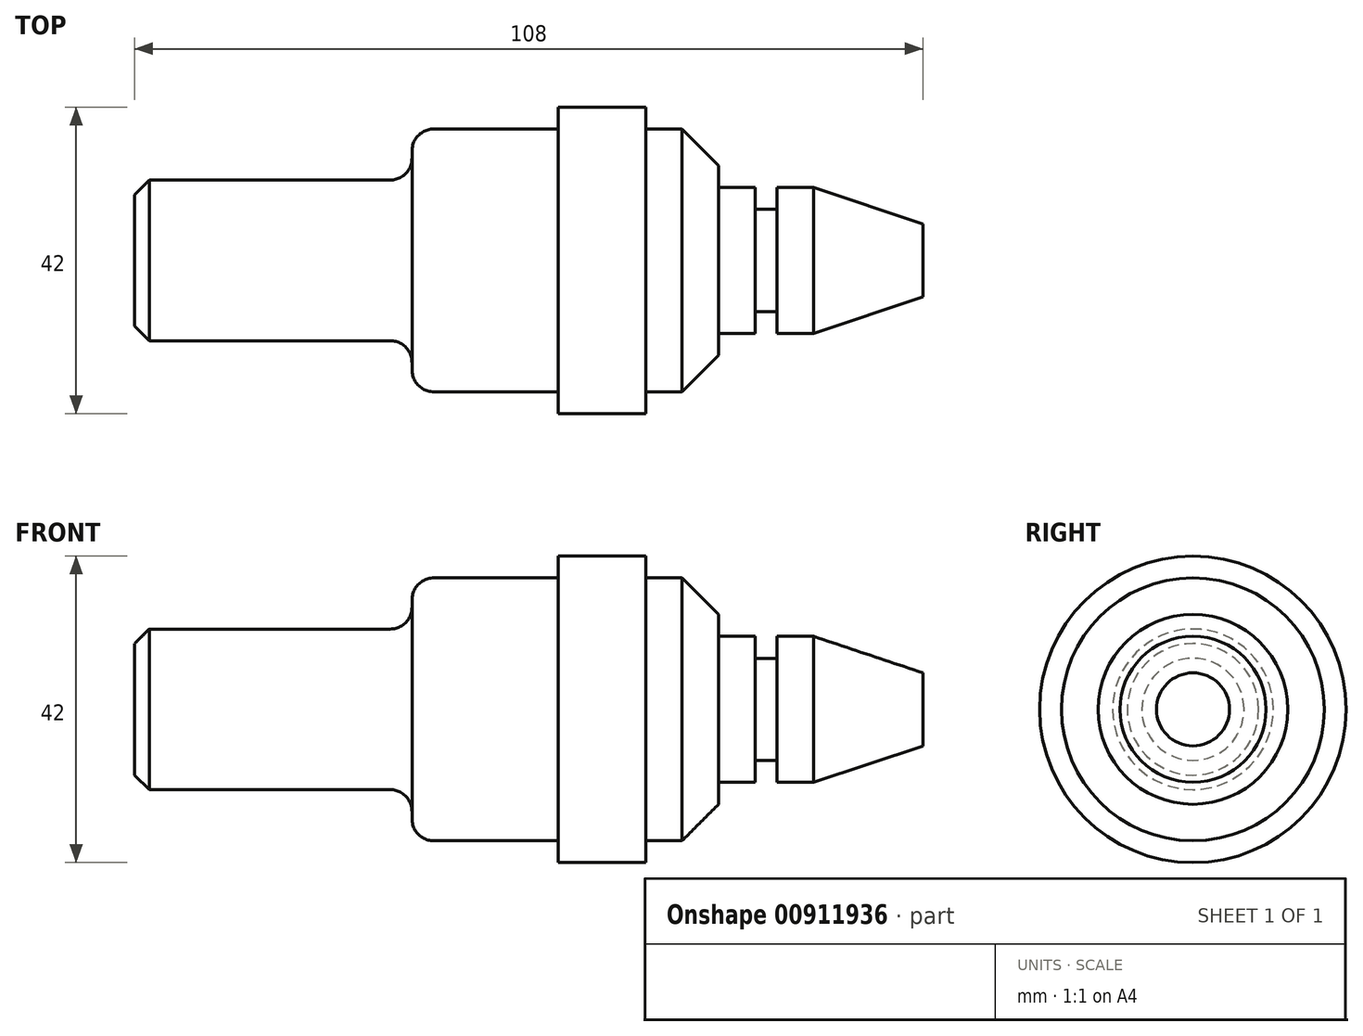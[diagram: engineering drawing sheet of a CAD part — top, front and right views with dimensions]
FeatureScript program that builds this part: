
annotation { "Feature Type Name" : "Feature", "Feature Type Description" : "" }
export const myFeature = defineFeature(function(context is Context, id is Id, definition is map)
    precondition{}
    {
        {
            var Q0;
            Q0=qCreatedBy(makeId("Top.planeOp"),FACE);
            var sketch = newSketch(context, id + "F0", { "sketchPlane" : qUnion([Q0])});
            skLineSegment(sketch, "E0", {"start": v(-211.25, 52.42) * mm, "end": v(-103.25, 52.42) * mm});
            skLineSegment(sketch, "E1", {"start": v(-211.25, 52.42) * mm, "end": v(-211.25, 41.42) * mm});
            skLineSegment(sketch, "E2", {"start": v(-211.25, 41.42) * mm, "end": v(-173.25, 41.42) * mm});
            skLineSegment(sketch, "E3", {"start": v(-173.25, 41.42) * mm, "end": v(-173.25, 34.42) * mm});
            skLineSegment(sketch, "E4", {"start": v(-173.25, 34.42) * mm, "end": v(-153.25, 34.42) * mm});
            skLineSegment(sketch, "E5", {"start": v(-153.25, 34.42) * mm, "end": v(-153.25, 31.42) * mm});
            skLineSegment(sketch, "E6", {"start": v(-153.25, 31.42) * mm, "end": v(-141.25, 31.42) * mm});
            skLineSegment(sketch, "E7", {"start": v(-141.25, 31.42) * mm, "end": v(-141.25, 34.42) * mm});
            skLineSegment(sketch, "E8", {"start": v(-141.25, 34.42) * mm, "end": v(-131.25, 34.42) * mm});
            skLineSegment(sketch, "E9", {"start": v(-131.25, 34.42) * mm, "end": v(-131.25, 42.42) * mm});
            skLineSegment(sketch, "E10", {"start": v(-131.25, 42.42) * mm, "end": v(-126.25, 42.42) * mm});
            skLineSegment(sketch, "E11", {"start": v(-126.25, 42.42) * mm, "end": v(-126.25, 45.42) * mm});
            skLineSegment(sketch, "E12", {"start": v(-126.25, 45.42) * mm, "end": v(-123.25, 45.42) * mm});
            skLineSegment(sketch, "E13", {"start": v(-123.25, 45.42) * mm, "end": v(-123.25, 42.42) * mm});
            skLineSegment(sketch, "E14", {"start": v(-123.25, 42.42) * mm, "end": v(-118.25, 42.42) * mm});
            skLineSegment(sketch, "E15", {"start": v(-118.25, 42.42) * mm, "end": v(-103.25, 47.42) * mm});
            skLineSegment(sketch, "E16", {"start": v(-103.25, 52.42) * mm, "end": v(-103.25, 47.42) * mm});
            skSolve(sketch);
        }
        {
            var Q0;
            Q0=makeQuery(id+"F0.imprint","IMPRINT",FACE,{"disambiguationData":[TD([[makeQuery(id+"F0.imprint","IMPRINT",EDGE,{"derivedFrom":sQuery(id+"F0.wireOp",EDGE,"E0")}),-1.0]])]});
            var Q1;
            Q1=sQuery(id+"F0.wireOp",EDGE,"E0");
            revolve(context, id + "F1", {"surfaceOperationType" : NewSurfaceOperationType.NEW, "entities" : qUnion([Q0]), "axis" : qUnion([Q1]), "revolveType" : RevolveType.FULL});
        }
        {
            var Q0;
            Q0=makeQuery(id+"F1.opRevolve","SWEPT_EDGE",EDGE,{"disambiguationData":[OSD([sQuery(id+"F0.wireOp",EDGE,"E1"),sQuery(id+"F0.wireOp",EDGE,"E2")])]});
            chamfer(context, id + "F2", {"entities" : qUnion([Q0]), "width" : 2 * mm});
        }
        {
            var Q0;
            Q0=makeQuery(id+"F1.opRevolve","SWEPT_EDGE",EDGE,{"disambiguationData":[OSD([sQuery(id+"F0.wireOp",EDGE,"E2"),sQuery(id+"F0.wireOp",EDGE,"E3")])]});
            var Q1;
            Q1=makeQuery(id+"F1.opRevolve","SWEPT_EDGE",EDGE,{"disambiguationData":[OSD([sQuery(id+"F0.wireOp",EDGE,"E3"),sQuery(id+"F0.wireOp",EDGE,"E4")])]});
            fillet(context, id + "F3", {"entities" : qUnion([Q0, Q1]), "radius" : 3 * mm, "tangentPropagation" : true, "allowEdgeOverflow" : false});
        }
        {
            var Q0;
            Q0=makeQuery(id+"F1.opRevolve","SWEPT_EDGE",EDGE,{"disambiguationData":[OSD([sQuery(id+"F0.wireOp",EDGE,"E8"),sQuery(id+"F0.wireOp",EDGE,"E9")])]});
            chamfer(context, id + "F4", {"entities" : qUnion([Q0]), "width" : 5 * mm, "tangentPropagation" : true});
        }
    });
